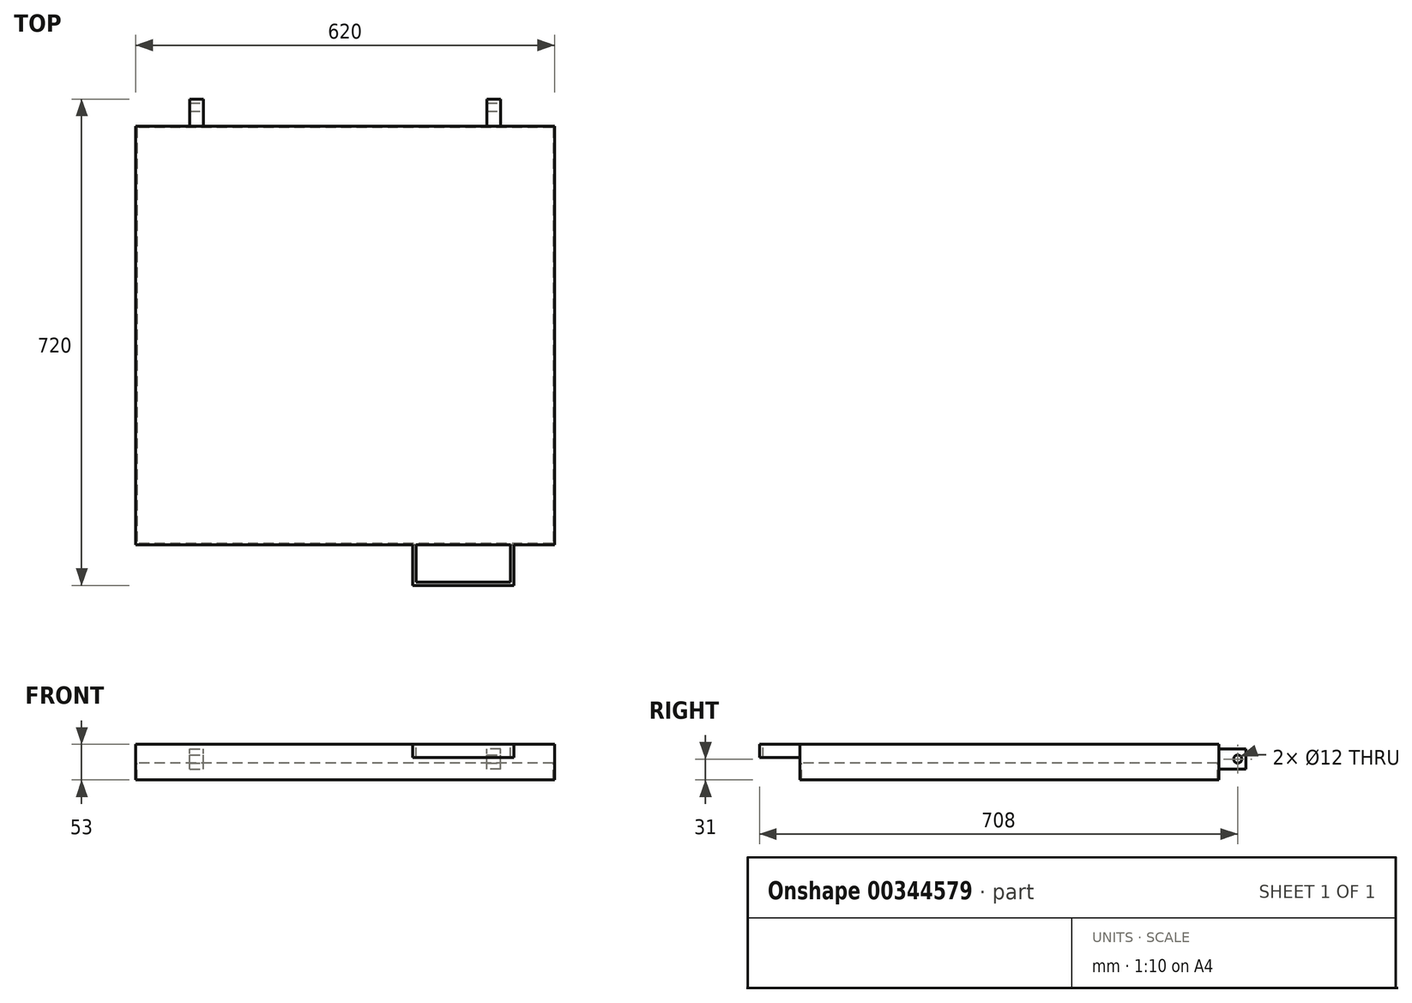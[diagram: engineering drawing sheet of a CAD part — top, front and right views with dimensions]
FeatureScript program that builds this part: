
annotation { "Feature Type Name" : "Feature", "Feature Type Description" : "" }
export const myFeature = defineFeature(function(context is Context, id is Id, definition is map)
    precondition{}
    {
        {
            var Q0;
            Q0=qCreatedBy(makeId("Top.planeOp"),FACE);
            var sketch = newSketch(context, id + "F0", { "sketchPlane" : qUnion([Q0])});
            skLineSegment(sketch, "E0.bottom", {"start": v(-310, 310) * mm, "end": v(310, 310) * mm});
            skLineSegment(sketch, "E0.top", {"start": v(-310, -310) * mm, "end": v(310, -310) * mm});
            skLineSegment(sketch, "E0.left", {"start": v(-310, 310) * mm, "end": v(-310, -310) * mm});
            skLineSegment(sketch, "E0.right", {"start": v(310, 310) * mm, "end": v(310, -310) * mm});
            skSolve(sketch);
        }
        {
            var Q0;
            Q0=makeQuery(id+"F0.imprint","IMPRINT",FACE,{"disambiguationData":[TD([[makeQuery(id+"F0.imprint","IMPRINT",EDGE,{"derivedFrom":sQuery(id+"F0.wireOp",EDGE,"E0.bottom")}),-1.0]])]});
            extrude(context, id + "F1", {"entities" : qUnion([Q0]), "depth" : 3 * mm});
        }
        {
            var Q0;
            Q0=makeQuery(id+"F1.opExtrude","CAP_FACE",FACE,{"disambiguationData":[OSD([sQuery(id+"F0.wireOp",EDGE,"E0.bottom"),sQuery(id+"F0.wireOp",EDGE,"E0.top"),sQuery(id+"F0.wireOp",EDGE,"E0.left"),sQuery(id+"F0.wireOp",EDGE,"E0.right")])],"isStart":true});
            var sketch = newSketch(context, id + "F2", { "sketchPlane" : qUnion([Q0])});
            skLineSegment(sketch, "E1.bottom", {"start": v(308, -308) * mm, "end": v(-308, -308) * mm});
            skLineSegment(sketch, "E1.top", {"start": v(308, 308) * mm, "end": v(-308, 308) * mm});
            skLineSegment(sketch, "E1.left", {"start": v(308, -308) * mm, "end": v(308, 308) * mm});
            skLineSegment(sketch, "E1.right", {"start": v(-308, -308) * mm, "end": v(-308, 308) * mm});
            skLineSegment(sketch, "E2.0", {"start": v(310, -310) * mm, "end": v(310, 310) * mm});
            skSolve(sketch);
        }
        {
            var Q0;
            Q0=makeQuery(id+"F2.imprint","IMPRINT",FACE,{"disambiguationData":[TD([[makeQuery(id+"F2.imprint","IMPRINT",EDGE,{"derivedFrom":sQuery(id+"F2.wireOp",EDGE,"E1.bottom")}),1.0]])]});
            extrude(context, id + "F3", {"entities" : qUnion([Q0]), "operationType" : NewBodyOperationType.ADD, "depth" : 25 * mm});
        }
        {
            var Q0;
            Q0=makeQuery(id+"F1.opExtrude","CAP_FACE",FACE,{"disambiguationData":[OSD([sQuery(id+"F0.wireOp",EDGE,"E0.bottom"),sQuery(id+"F0.wireOp",EDGE,"E0.top"),sQuery(id+"F0.wireOp",EDGE,"E0.left"),sQuery(id+"F0.wireOp",EDGE,"E0.right")])],"isStart":false});
            extrude(context, id + "F4", {"entities" : qUnion([Q0]), "operationType" : NewBodyOperationType.ADD, "depth" : 25 * mm});
        }
        {
            var Q0;
            {var subQ0=sQuery(id+"F0.wireOp",EDGE,"E0.top");Q0=makeQuery(id+"F4.boolean.opBoolean","MERGE",FACE,{"derivedFrom":[makeQuery(id+"F3.boolean.opBoolean","MERGE",FACE,{"derivedFrom":[makeQuery(id+"F1.opExtrude","SWEPT_FACE",FACE,{"disambiguationData":[OSD([subQ0])]}),makeQuery(id+"F3.opExtrude","SWEPT_FACE",FACE,{"disambiguationData":[OSD([subQ0])]})]}),makeQuery(id+"F4.opExtrude","SWEPT_FACE",FACE,{"disambiguationData":[OSD([subQ0])]})]});}
            var sketch = newSketch(context, id + "F5", { "sketchPlane" : qUnion([Q0])});
            skLineSegment(sketch, "E3.bottom", {"start": v(250, 28) * mm, "end": v(100, 28) * mm});
            skLineSegment(sketch, "E3.top", {"start": v(250, 8) * mm, "end": v(100, 8) * mm});
            skLineSegment(sketch, "E3.left", {"start": v(250, 28) * mm, "end": v(250, 8) * mm});
            skLineSegment(sketch, "E3.right", {"start": v(100, 28) * mm, "end": v(100, 8) * mm});
            skSolve(sketch);
        }
        {
            var Q0;
            Q0=makeQuery(id+"F5.imprint","IMPRINT",FACE,{"disambiguationData":[TD([[makeQuery(id+"F5.imprint","IMPRINT",EDGE,{"derivedFrom":sQuery(id+"F5.wireOp",EDGE,"E3.bottom")}),-1.0]])]});
            extrude(context, id + "F6", {"entities" : qUnion([Q0]), "operationType" : NewBodyOperationType.ADD, "depth" : 60 * mm});
        }
        {
            var Q0;
            Q0=makeQuery(id+"F6.boolean.opBoolean","MERGE",FACE,{"derivedFrom":[makeQuery(id+"F4.opExtrude","CAP_FACE",FACE,{"disambiguationData":[OSD([sQuery(id+"F0.wireOp",EDGE,"E0.bottom"),sQuery(id+"F0.wireOp",EDGE,"E0.top"),sQuery(id+"F0.wireOp",EDGE,"E0.left"),sQuery(id+"F0.wireOp",EDGE,"E0.right")])],"isStart":false}),makeQuery(id+"F6.opExtrude","SWEPT_FACE",FACE,{"disambiguationData":[OSD([sQuery(id+"F5.wireOp",EDGE,"E3.bottom")])]})]});
            var sketch = newSketch(context, id + "F7", { "sketchPlane" : qUnion([Q0])});
            skLineSegment(sketch, "E4.bottom", {"start": v(105, -310) * mm, "end": v(245, -310) * mm});
            skLineSegment(sketch, "E4.top", {"start": v(105, -365) * mm, "end": v(245, -365) * mm});
            skLineSegment(sketch, "E4.left", {"start": v(105, -310) * mm, "end": v(105, -365) * mm});
            skLineSegment(sketch, "E4.right", {"start": v(245, -310) * mm, "end": v(245, -365) * mm});
            skSolve(sketch);
        }
        {
            var Q0;
            Q0=makeQuery(id+"F7.imprint","IMPRINT",FACE,{"disambiguationData":[TD([[makeQuery(id+"F7.imprint","IMPRINT",EDGE,{"derivedFrom":sQuery(id+"F7.wireOp",EDGE,"E4.bottom")}),-1.0]])]});
            extrude(context, id + "F8", {"entities" : qUnion([Q0]), "operationType" : NewBodyOperationType.REMOVE, "oppositeDirection" : true, "depth" : 25 * mm});
        }
        {
            var Q0;
            {var subQ0=sQuery(id+"F0.wireOp",EDGE,"E0.bottom");Q0=makeQuery(id+"F4.boolean.opBoolean","MERGE",FACE,{"derivedFrom":[makeQuery(id+"F3.boolean.opBoolean","MERGE",FACE,{"derivedFrom":[makeQuery(id+"F1.opExtrude","SWEPT_FACE",FACE,{"disambiguationData":[OSD([subQ0])]}),makeQuery(id+"F3.opExtrude","SWEPT_FACE",FACE,{"disambiguationData":[OSD([subQ0])]})]}),makeQuery(id+"F4.opExtrude","SWEPT_FACE",FACE,{"disambiguationData":[OSD([subQ0])]})]});}
            var sketch = newSketch(context, id + "F9", { "sketchPlane" : qUnion([Q0])});
            skLineSegment(sketch, "E5.bottom", {"start": v(230, -9) * mm, "end": v(210, -9) * mm});
            skLineSegment(sketch, "E5.top", {"start": v(230, 21) * mm, "end": v(210, 21) * mm});
            skLineSegment(sketch, "E5.left", {"start": v(230, -9) * mm, "end": v(230, 21) * mm});
            skLineSegment(sketch, "E5.right", {"start": v(210, -9) * mm, "end": v(210, 21) * mm});
            skLineSegment(sketch, "E6.MirrorCS", {"start": v(-230, -9) * mm, "end": v(-210, -9) * mm});
            skLineSegment(sketch, "E7.MirrorCS", {"start": v(-230, -9) * mm, "end": v(-230, 21) * mm});
            skLineSegment(sketch, "E8.MirrorCS", {"start": v(-230, 21) * mm, "end": v(-210, 21) * mm});
            skLineSegment(sketch, "E9.MirrorCS", {"start": v(-210, -9) * mm, "end": v(-210, 21) * mm});
            skSolve(sketch);
        }
        {
            var Q0;
            Q0=makeQuery(id+"F9.imprint","IMPRINT",FACE,{"disambiguationData":[TD([[makeQuery(id+"F9.imprint","IMPRINT",EDGE,{"derivedFrom":sQuery(id+"F9.wireOp",EDGE,"E5.bottom")}),-1.0]])]});
            var Q1;
            Q1=makeQuery(id+"F9.imprint","IMPRINT",FACE,{"disambiguationData":[TD([[makeQuery(id+"F9.imprint","IMPRINT",EDGE,{"derivedFrom":sQuery(id+"F9.wireOp",EDGE,"E6.MirrorCS")}),1.0]])]});
            extrude(context, id + "F10", {"entities" : qUnion([Q0, Q1]), "operationType" : NewBodyOperationType.ADD, "depth" : 40 * mm});
        }
        {
            var Q0;
            Q0=makeQuery(id+"F10.opExtrude","SWEPT_FACE",FACE,{"disambiguationData":[OSD([sQuery(id+"F9.wireOp",EDGE,"E7.MirrorCS")])]});
            var sketch = newSketch(context, id + "F11", { "sketchPlane" : qUnion([Q0])});
            skCircle(sketch, "E10", {"center": v(338, 6) * mm, "radius": 6 * mm});
            skPoint(sketch, "E10.centerSnap0", {"position": v(350, 6) * mm});
            skSolve(sketch);
        }
        {
            var Q0;
            Q0=makeQuery(id+"F11.imprint","IMPRINT",FACE,{"disambiguationData":[TD([[makeQuery(id+"F11.imprint","IMPRINT",EDGE,{"derivedFrom":sQuery(id+"F11.wireOp",EDGE,"E10")}),1.0]])]});
            extrude(context, id + "F12", {"entities" : qUnion([Q0]), "operationType" : NewBodyOperationType.REMOVE, "endBound" : BoundingType.THROUGH_ALL, "oppositeDirection" : true, "depth" : 25 * mm});
        }
    });
